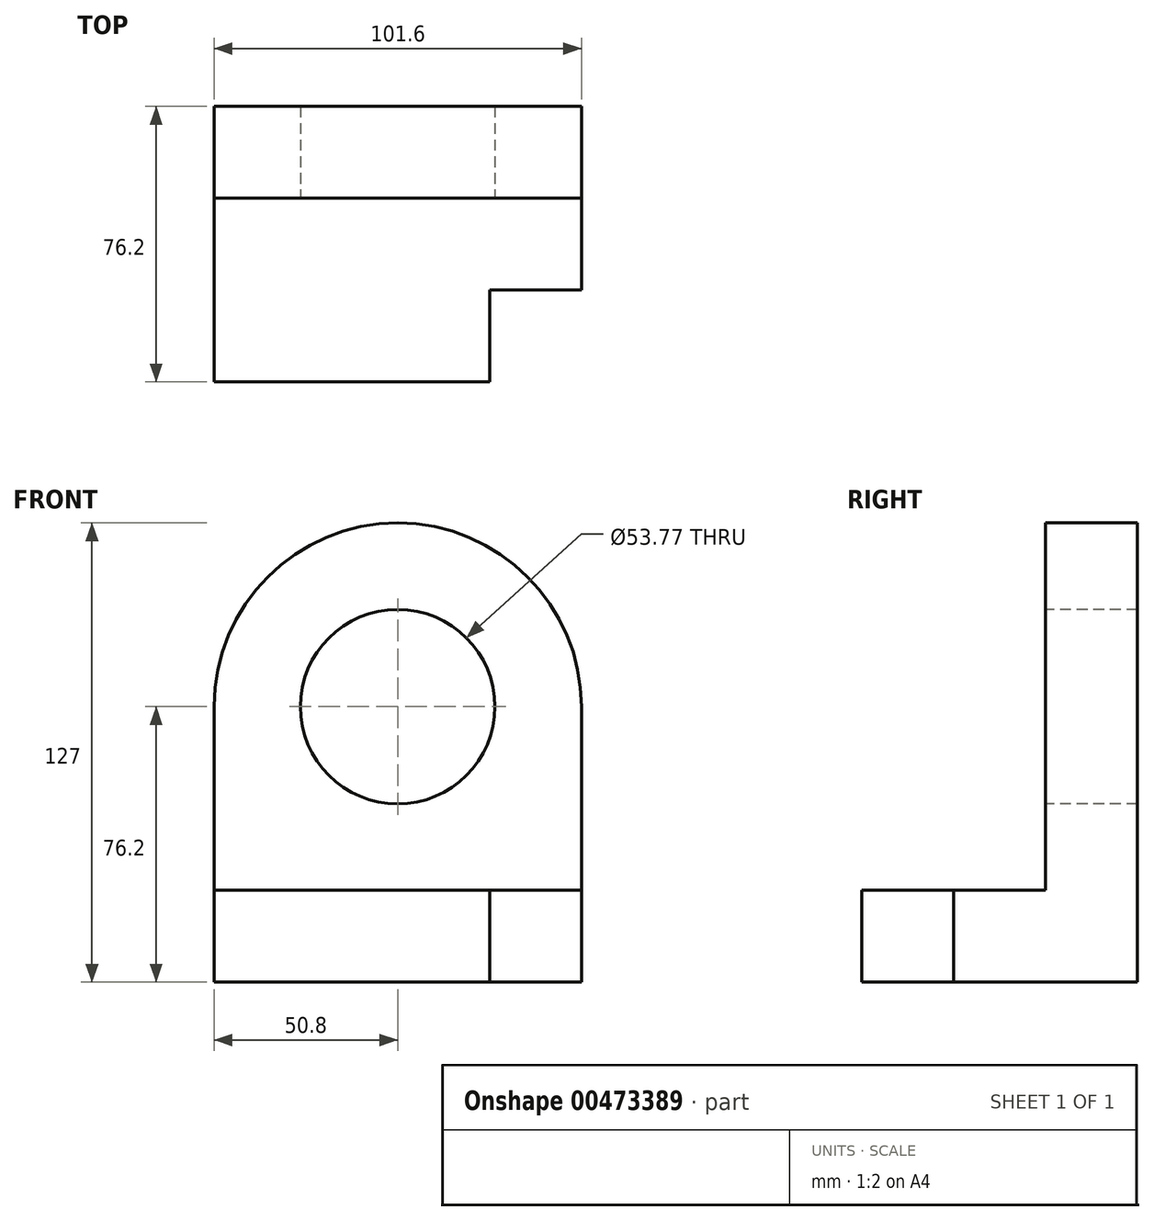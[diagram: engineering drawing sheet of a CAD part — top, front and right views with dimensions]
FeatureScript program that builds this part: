
annotation { "Feature Type Name" : "Feature", "Feature Type Description" : "" }
export const myFeature = defineFeature(function(context is Context, id is Id, definition is map)
    precondition{}
    {
        {
            var Q0;
            Q0=qCreatedBy(makeId("Top.planeOp"),FACE);
            var sketch = newSketch(context, id + "F0", { "sketchPlane" : qUnion([Q0])});
            skLineSegment(sketch, "E0.bottom", {"start": v(50.8, 38.1) * mm, "end": v(-50.8, 38.1) * mm});
            skLineSegment(sketch, "E0.top", {"start": v(50.8, -38.1) * mm, "end": v(-50.8, -38.1) * mm});
            skLineSegment(sketch, "E0.left", {"start": v(50.8, 38.1) * mm, "end": v(50.8, -38.1) * mm});
            skLineSegment(sketch, "E0.right", {"start": v(-50.8, 38.1) * mm, "end": v(-50.8, -38.1) * mm});
            skPoint(sketch, "E0.middle", {"position": v(0, 0) * mm});
            skSolve(sketch);
        }
        {
            var Q0;
            Q0=makeQuery(id+"F0.imprint","IMPRINT",FACE,{"disambiguationData":[TD([[makeQuery(id+"F0.imprint","IMPRINT",EDGE,{"derivedFrom":sQuery(id+"F0.wireOp",EDGE,"E0.bottom")}),1.0]])]});
            extrude(context, id + "F1", {"entities" : qUnion([Q0]), "depth" : 25.4 * mm});
        }
        {
            var Q0;
            Q0=makeQuery(id+"F1.opExtrude","CAP_FACE",FACE,{"disambiguationData":[OSD([sQuery(id+"F0.wireOp",EDGE,"E0.bottom"),sQuery(id+"F0.wireOp",EDGE,"E0.top"),sQuery(id+"F0.wireOp",EDGE,"E0.left"),sQuery(id+"F0.wireOp",EDGE,"E0.right")])],"isStart":false});
            var sketch = newSketch(context, id + "F2", { "sketchPlane" : qUnion([Q0])});
            skLineSegment(sketch, "E1.bottom", {"start": v(50.8, -38.1) * mm, "end": v(25.4, -38.1) * mm});
            skLineSegment(sketch, "E1.top", {"start": v(50.8, -12.7) * mm, "end": v(25.4, -12.7) * mm});
            skLineSegment(sketch, "E1.left", {"start": v(50.8, -38.1) * mm, "end": v(50.8, -12.7) * mm});
            skLineSegment(sketch, "E1.right", {"start": v(25.4, -38.1) * mm, "end": v(25.4, -12.7) * mm});
            skSolve(sketch);
        }
        {
            var Q0;
            Q0=makeQuery(id+"F2.imprint","IMPRINT",FACE,{"disambiguationData":[TD([[makeQuery(id+"F2.imprint","IMPRINT",EDGE,{"derivedFrom":sQuery(id+"F2.wireOp",EDGE,"E1.bottom")}),-1.0]])]});
            extrude(context, id + "F3", {"entities" : qUnion([Q0]), "operationType" : NewBodyOperationType.REMOVE, "endBound" : BoundingType.THROUGH_ALL, "oppositeDirection" : true, "depth" : 25.4 * mm});
        }
        {
            var Q0;
            Q0=makeQuery(id+"F1.opExtrude","CAP_FACE",FACE,{"disambiguationData":[OSD([sQuery(id+"F0.wireOp",EDGE,"E0.bottom"),sQuery(id+"F0.wireOp",EDGE,"E0.top"),sQuery(id+"F0.wireOp",EDGE,"E0.left"),sQuery(id+"F0.wireOp",EDGE,"E0.right")])],"isStart":false});
            var sketch = newSketch(context, id + "F4", { "sketchPlane" : qUnion([Q0])});
            skLineSegment(sketch, "E2.bottom", {"start": v(-50.8, 38.1) * mm, "end": v(50.8, 38.1) * mm});
            skLineSegment(sketch, "E2.top", {"start": v(-50.8, 12.7) * mm, "end": v(50.8, 12.7) * mm});
            skLineSegment(sketch, "E2.left", {"start": v(-50.8, 38.1) * mm, "end": v(-50.8, 12.7) * mm});
            skLineSegment(sketch, "E2.right", {"start": v(50.8, 38.1) * mm, "end": v(50.8, 12.7) * mm});
            skSolve(sketch);
        }
        {
            var Q0;
            Q0=makeQuery(id+"F4.imprint","IMPRINT",FACE,{"disambiguationData":[TD([[makeQuery(id+"F4.imprint","IMPRINT",EDGE,{"derivedFrom":sQuery(id+"F4.wireOp",EDGE,"E2.bottom")}),1.0]])]});
            extrude(context, id + "F5", {"entities" : qUnion([Q0]), "operationType" : NewBodyOperationType.ADD, "depth" : 101.6 * mm});
        }
        {
            var Q0;
            Q0=makeQuery(id+"F5.opExtrude","CAP_EDGE",EDGE,{"disambiguationData":[OSD([sQuery(id+"F4.wireOp",EDGE,"E2.left")])],"isStart":false});
            fillet(context, id + "F6", {"entities" : qUnion([Q0]), "radius" : 50.8 * mm, "tangentPropagation" : true, "allowEdgeOverflow" : false});
        }
        {
            var Q0;
            Q0=makeQuery(id+"F5.opExtrude","CAP_EDGE",EDGE,{"disambiguationData":[OSD([sQuery(id+"F4.wireOp",EDGE,"E2.right")])],"isStart":false});
            fillet(context, id + "F7", {"entities" : qUnion([Q0]), "radius" : 50.8 * mm, "tangentPropagation" : true, "allowEdgeOverflow" : false});
        }
        {
            var Q0;
            Q0=makeQuery(id+"F5.opExtrude","SWEPT_FACE",FACE,{"disambiguationData":[OSD([sQuery(id+"F4.wireOp",EDGE,"E2.top")])]});
            var sketch = newSketch(context, id + "F8", { "sketchPlane" : qUnion([Q0])});
            skCircle(sketch, "E3", {"center": v(0, 76.2) * mm, "radius": 26.89 * mm});
            skSolve(sketch);
        }
        {
            var Q0;
            Q0=makeQuery(id+"F8.imprint","IMPRINT",FACE,{"disambiguationData":[TD([[makeQuery(id+"F8.imprint","IMPRINT",EDGE,{"derivedFrom":sQuery(id+"F8.wireOp",EDGE,"E3")}),1.0]])]});
            extrude(context, id + "F9", {"entities" : qUnion([Q0]), "operationType" : NewBodyOperationType.REMOVE, "endBound" : BoundingType.THROUGH_ALL, "oppositeDirection" : true, "depth" : 25.4 * mm});
        }
    });
